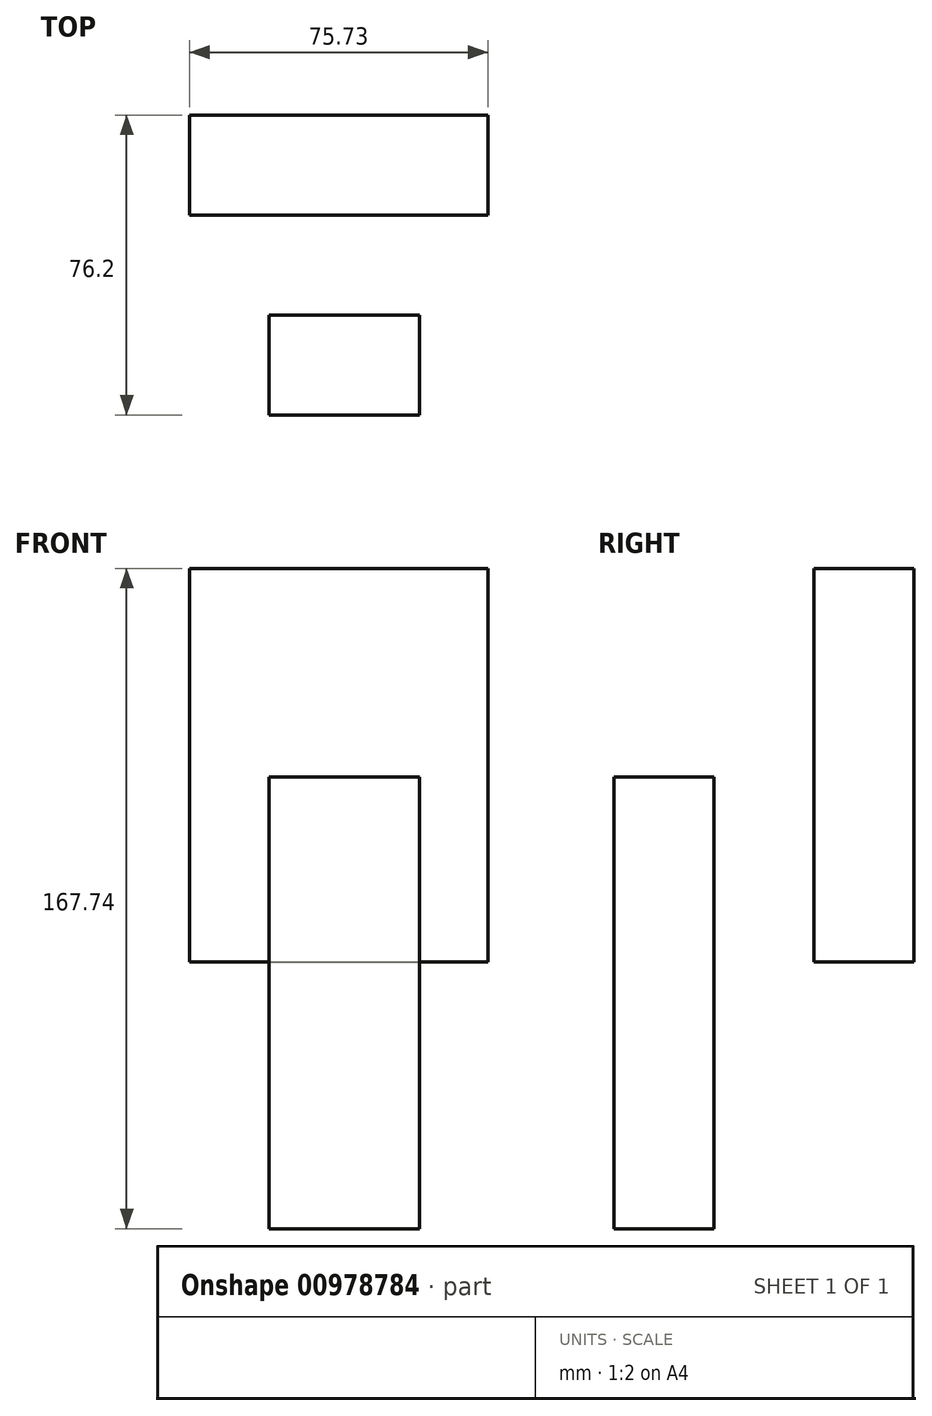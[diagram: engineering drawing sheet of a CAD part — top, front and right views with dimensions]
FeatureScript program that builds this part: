
annotation { "Feature Type Name" : "Feature", "Feature Type Description" : "" }
export const myFeature = defineFeature(function(context is Context, id is Id, definition is map)
    precondition{}
    {
        {
            var Q0;
            Q0=qCreatedBy(makeId("Front.planeOp"),FACE);
            var sketch = newSketch(context, id + "F0", { "sketchPlane" : qUnion([Q0])});
            skLineSegment(sketch, "E0.bottom", {"start": v(-34.3, 37.12) * mm, "end": v(41.43, 37.12) * mm});
            skLineSegment(sketch, "E0.top", {"start": v(-34.3, -62.8) * mm, "end": v(41.43, -62.8) * mm});
            skLineSegment(sketch, "E0.left", {"start": v(-34.3, 37.12) * mm, "end": v(-34.3, -62.8) * mm});
            skLineSegment(sketch, "E0.right", {"start": v(41.43, 37.12) * mm, "end": v(41.43, -62.8) * mm});
            skSolve(sketch);
        }
        {
            var Q0;
            Q0=makeQuery(id+"F0.imprint","IMPRINT",FACE,{"disambiguationData":[TD([[makeQuery(id+"F0.imprint","IMPRINT",EDGE,{"derivedFrom":sQuery(id+"F0.wireOp",EDGE,"E0.bottom")}),-1.0]])]});
            extrude(context, id + "F1", {"entities" : qUnion([Q0]), "depth" : 25.4 * mm, "offsetDistance" : 25.4 * mm});
        }
        {
            var Q0;
            Q0=makeQuery(id+"F1.opExtrude","CAP_FACE",FACE,{"disambiguationData":[OSD([sQuery(id+"F0.wireOp",EDGE,"E0.bottom"),sQuery(id+"F0.wireOp",EDGE,"E0.top"),sQuery(id+"F0.wireOp",EDGE,"E0.left"),sQuery(id+"F0.wireOp",EDGE,"E0.right")])],"isStart":false});
            cPlane(context, id + "F2", {"entities" : qUnion([Q0]), "cplaneType" : CPlaneType.OFFSET, "offset" : 25.4 * mm, "width" : 152.4 * mm, "height" : 152.4 * mm});
        }
        {
            var Q0;
            Q0=qCreatedBy(id+"F2.planeOp",FACE);
            var sketch = newSketch(context, id + "F3", { "sketchPlane" : qUnion([Q0])});
            skLineSegment(sketch, "E1.bottom", {"start": v(-14.18, -15.85) * mm, "end": v(24.06, -15.85) * mm});
            skLineSegment(sketch, "E1.top", {"start": v(-14.18, -130.62) * mm, "end": v(24.06, -130.62) * mm});
            skLineSegment(sketch, "E1.left", {"start": v(-14.18, -15.85) * mm, "end": v(-14.18, -130.62) * mm});
            skLineSegment(sketch, "E1.right", {"start": v(24.06, -15.85) * mm, "end": v(24.06, -130.62) * mm});
            skSolve(sketch);
        }
        {
            var Q0;
            Q0=makeQuery(id+"F3.imprint","IMPRINT",FACE,{"disambiguationData":[TD([[makeQuery(id+"F3.imprint","IMPRINT",EDGE,{"derivedFrom":sQuery(id+"F3.wireOp",EDGE,"E1.bottom")}),-1.0]])]});
            extrude(context, id + "F4", {"entities" : qUnion([Q0]), "depth" : 25.4 * mm, "offsetDistance" : 25.4 * mm});
        }
    });
